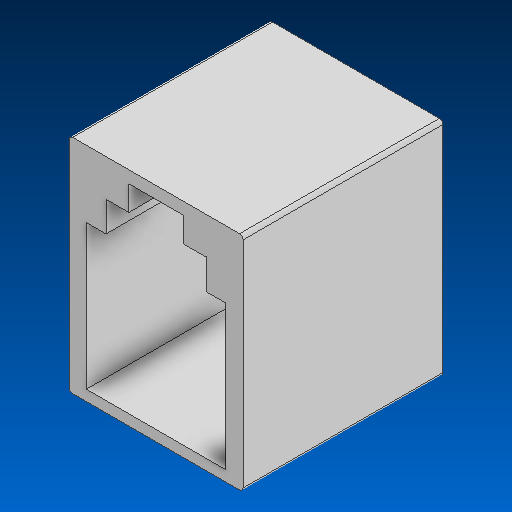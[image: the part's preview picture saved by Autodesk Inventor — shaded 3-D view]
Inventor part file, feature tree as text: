
AUTODESK INVENTOR PART (.ipt)
format: ipt  version: 2022.2 (Build 262287000, 287)  size: 100,352 bytes
history: native  units: in
note: dims shown in document units (in); Inventor stores cm internally (conversion verified against a paired STEP export)
features: fillet x1
ambient origin geometry x8: Origin, YZ Plane, XZ Plane, XY Plane, X Axis, Y Axis, Z Axis, Center Point
bodies: Solid1 (feature_tree)
feature tree (1):
  fillet  "Fillet1"  [1 undecoded]
note: 1 required parameter value undecoded (feature->parameter linkage not recoverable at this tier; creation-order binding heuristic only, values carry confidence <= 0.55)
